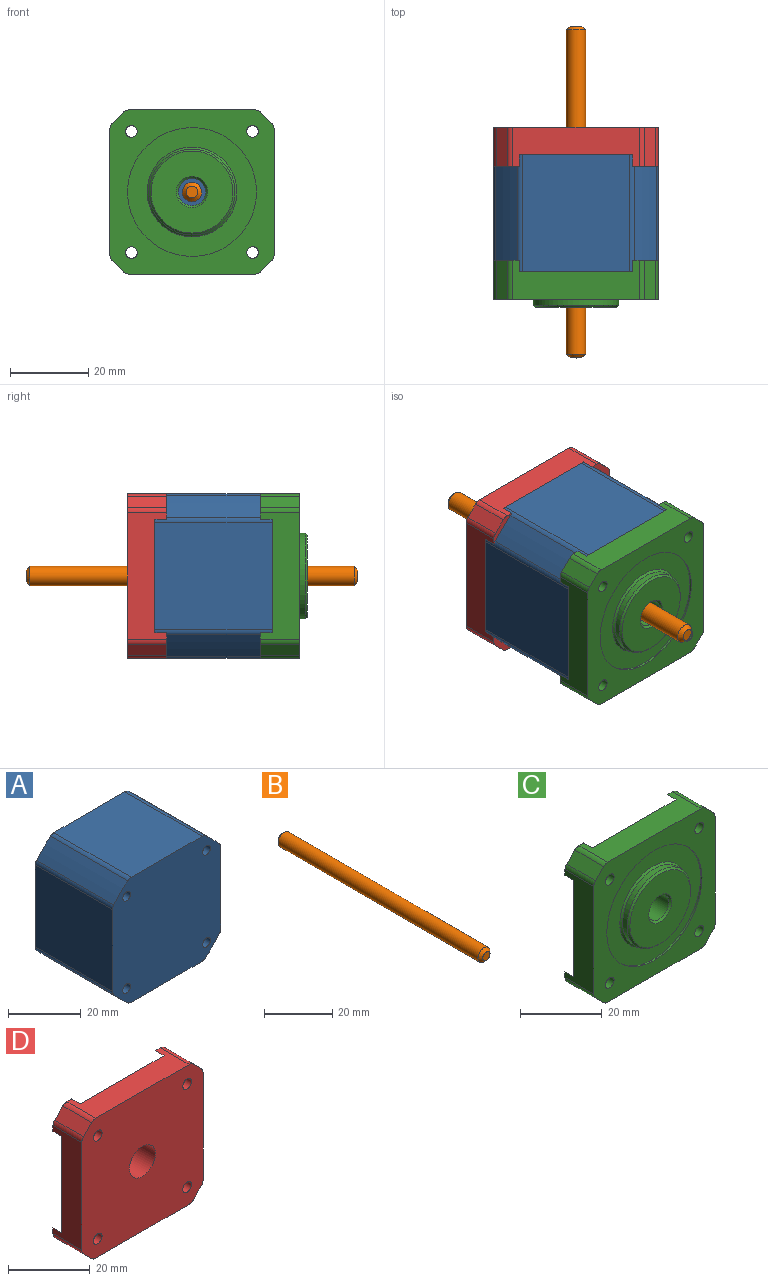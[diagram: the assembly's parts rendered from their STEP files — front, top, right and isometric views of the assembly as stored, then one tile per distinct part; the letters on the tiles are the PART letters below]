
ASSEMBLY  parts=4 mates=3
PART A: 22 faces, bbox 42x30x42 mm
  f0: cylinder r=55mm len=30mm, axis (0,1,0), area 230.4mm2, adj f8,f9,f10,f17
  f1: plane 30x27.54mm, normal (1,0,0), area 826.2mm2, adj f8,f9,f10,f11
  f2: cylinder r=55mm len=30mm, axis (0,1,0), area 230.4mm2, adj f8,f9,f11,f12
  f3: plane 30x27.54mm, normal (0,0,1), area 826.2mm2, adj f8,f9,f12,f13
  f4: cylinder r=55mm len=30mm, axis (0,1,0), area 230.4mm2, adj f8,f9,f13,f14
  f5: plane 30x27.54mm, normal (-1,0,0), area 826.2mm2, adj f8,f9,f14,f15
  f6: cylinder r=55mm len=30mm, axis (0,1,0), area 230.4mm2, adj f8,f9,f15,f16
  f7: plane 30x27.54mm, normal (0,0,-1), area 826.2mm2, adj f8,f9,f16,f17
  f8: plane 42x42mm, normal (0,-1,0), area 1655.7mm2, adj f0,f1,f2,f3,f4,f5,f6,f7
  f9: plane 42x42mm, normal (0,1,0), area 1655.7mm2, adj f0,f1,f2,f3,f4,f5,f6,f7
  f10: cylinder r=2mm len=30mm, axis (0,1,0), area 42.9mm2, adj f0,f1,f8,f9
  f11: cylinder r=2mm len=30mm, axis (0,1,0), area 42.9mm2, adj f1,f2,f8,f9
  f12: cylinder r=2mm len=30mm, axis (0,1,0), area 42.9mm2, adj f2,f3,f8,f9
  f13: cylinder r=2mm len=30mm, axis (0,1,0), area 42.9mm2, adj f3,f4,f8,f9
  f14: cylinder r=2mm len=30mm, axis (0,1,0), area 42.9mm2, adj f4,f5,f8,f9
  f15: cylinder r=2mm len=30mm, axis (0,1,0), area 42.9mm2, adj f5,f6,f8,f9
  f16: cylinder r=2mm len=30mm, axis (0,1,0), area 42.9mm2, adj f6,f7,f8,f9
  f17: cylinder r=2mm len=30mm, axis (0,1,0), area 42.9mm2, adj f0,f7,f8,f9
  f18: cylinder r=1.5mm len=30mm, axis (0,-1,0), area 282.7mm2, adj f8,f9
  f19: cylinder r=1.5mm len=30mm, axis (0,-1,0), area 282.7mm2, adj f8,f9
  f20: cylinder r=1.5mm len=30mm, axis (0,-1,0), area 282.7mm2, adj f8,f9
  f21: cylinder r=1.5mm len=30mm, axis (0,-1,0), area 282.7mm2, adj f8,f9
PART B: 5 faces, bbox 5x85x5 mm
  f0: cylinder r=2.5mm len=83mm, axis (0,1,0), area 1303.8mm2, adj f3,f4
  f1: plane 3x3mm, normal (0,-1,0), area 7.1mm2, adj f4
  f2: plane 3x3mm, normal (0,1,0), area 7.1mm2, adj f3
  f3: cone r=2.5mm half-angle=45deg, axis (0,-1,0), area 17.8mm2, adj f0,f2
  f4: cone r=1.5mm half-angle=45deg, axis (0,1,0), area 17.8mm2, adj f0,f1
PART C: 38 faces, bbox 42x12x42 mm
  f0: plane 32.34x10mm, normal (1,0,0), area 236.4mm2, adj f3,f4,f9,f20,f21,f29,f31,f32
  f1: plane 32.34x10mm, normal (0,0,1), area 236.4mm2, adj f2,f3,f9,f18,f19,f29,f30,f31
  f2: plane 6.49x6.49mm, normal (0,1,0), area 11.7mm2, adj f1,f7,f13,f19,f23,f30
  f3: plane 6.49x6.49mm, normal (0,1,0), area 11.7mm2, adj f0,f1,f12,f18,f21,f31
  f4: plane 6.49x6.49mm, normal (0,1,0), area 11.7mm2, adj f0,f8,f11,f20,f25,f32
  f5: plane 6.49x6.49mm, normal (0,1,0), area 11.7mm2, adj f7,f8,f10,f22,f24,f33
  f6: cylinder r=3.5mm len=8.5mm, axis (0,-1,0), area 186.9mm2, adj f27,f29
  f7: plane 32.34x10mm, normal (-1,0,0), area 236.4mm2, adj f2,f5,f9,f22,f23,f29,f30,f33
  f8: plane 32.34x10mm, normal (0,0,-1), area 236.4mm2, adj f4,f5,f9,f24,f25,f29,f32,f33
  f9: plane 42x42mm, normal (0,-1,0), area 847.7mm2, adj f0,f1,f7,f8,f10,f11,f12,f13
  f10: plane 10x2.83mm, normal (-0.71,0,-0.71), area 40mm2, adj f5,f9,f22,f24
  f11: plane 10x2.83mm, normal (0.71,0,-0.71), area 40mm2, adj f4,f9,f20,f25
  f12: plane 10x2.83mm, normal (0.71,0,0.71), area 40mm2, adj f3,f9,f18,f21
  f13: plane 10x2.83mm, normal (-0.71,0,0.71), area 40mm2, adj f2,f9,f19,f23
  f14: cylinder r=16.5mm len=33mm, axis (0,-1,0), area 51.8mm2, adj f9,f15
  f15: plane 33x33mm, normal (0,-1,0), area 439.8mm2, adj f14,f26
  f16: cylinder r=11mm len=22mm, axis (0,1,0), area 103.7mm2, adj f26,f28
  f17: plane 21x21mm, normal (0,-1,0), area 296.1mm2, adj f27,f28
  f18: cylinder r=2mm len=10mm, axis (0,-1,0), area 15.7mm2, adj f1,f3,f9,f12
  f19: cylinder r=2mm len=10mm, axis (0,-1,0), area 15.7mm2, adj f1,f2,f9,f13
  f20: cylinder r=2mm len=10mm, axis (0,1,0), area 15.7mm2, adj f0,f4,f9,f11
  f21: cylinder r=2mm len=10mm, axis (0,1,0), area 15.7mm2, adj f0,f3,f9,f12
  f22: cylinder r=2mm len=10mm, axis (0,-1,0), area 15.7mm2, adj f5,f7,f9,f10
  f23: cylinder r=2mm len=10mm, axis (0,-1,0), area 15.7mm2, adj f2,f7,f9,f13
  f24: cylinder r=2mm len=10mm, axis (0,1,0), area 15.7mm2, adj f5,f8,f9,f10
  f25: cylinder r=2mm len=10mm, axis (0,1,0), area 15.7mm2, adj f4,f8,f9,f11
  f26: cone r=11mm half-angle=45deg, axis (0,1,0), area 50mm2, adj f15,f16
  f27: cone r=3.5mm half-angle=45deg, axis (0,-1,0), area 16.7mm2, adj f6,f17
  f28: cone r=10.5mm half-angle=45deg, axis (0,1,0), area 47.8mm2, adj f16,f17
  f29: plane 42x42mm, normal (0,1,0), area 1617.7mm2, adj f0,f1,f6,f7,f8,f30,f31,f32
  f30: cylinder r=55mm len=6.49mm, axis (0,1,0), area 27.6mm2, adj f1,f2,f7,f29
  f31: cylinder r=55mm len=6.49mm, axis (0,1,0), area 27.6mm2, adj f0,f1,f3,f29
  f32: cylinder r=55mm len=6.49mm, axis (0,1,0), area 27.6mm2, adj f0,f4,f8,f29
  f33: cylinder r=55mm len=6.49mm, axis (0,1,0), area 27.6mm2, adj f5,f7,f8,f29
  f34: cylinder r=1.5mm len=7mm, axis (0,-1,0), area 66mm2, adj f9,f29
  f35: cylinder r=1.5mm len=7mm, axis (0,-1,0), area 66mm2, adj f9,f29
  f36: cylinder r=1.5mm len=7mm, axis (0,-1,0), area 66mm2, adj f9,f29
  f37: cylinder r=1.5mm len=7mm, axis (0,-1,0), area 66mm2, adj f9,f29
PART D: 31 faces, bbox 42x10x42 mm
  f0: plane 32.34x10mm, normal (1,0,0), area 236.4mm2, adj f3,f4,f8,f15,f16,f22,f23,f25
  f1: plane 32.34x10mm, normal (0,0,1), area 236.4mm2, adj f2,f3,f8,f13,f14,f21,f22,f25
  f2: plane 6.49x6.49mm, normal (0,1,0), area 11.7mm2, adj f1,f6,f12,f14,f18,f21
  f3: plane 6.49x6.49mm, normal (0,1,0), area 11.7mm2, adj f0,f1,f11,f13,f16,f22
  f4: plane 6.49x6.49mm, normal (0,1,0), area 11.7mm2, adj f0,f7,f10,f15,f20,f23
  f5: plane 6.49x6.49mm, normal (0,1,0), area 11.7mm2, adj f6,f7,f9,f17,f19,f24
  f6: plane 32.34x10mm, normal (-1,0,0), area 236.4mm2, adj f2,f5,f8,f17,f18,f21,f24,f25
  f7: plane 32.34x10mm, normal (0,0,-1), area 236.4mm2, adj f4,f5,f8,f19,f20,f23,f24,f25
  f8: plane 42x42mm, normal (0,-1,0), area 1639.4mm2, adj f0,f1,f6,f7,f9,f10,f11,f12
  f9: plane 10x2.83mm, normal (-0.71,0,-0.71), area 40mm2, adj f5,f8,f17,f19
  f10: plane 10x2.83mm, normal (0.71,0,-0.71), area 40mm2, adj f4,f8,f15,f20
  f11: plane 10x2.83mm, normal (0.71,0,0.71), area 40mm2, adj f3,f8,f13,f16
  f12: plane 10x2.83mm, normal (-0.71,0,0.71), area 40mm2, adj f2,f8,f14,f18
  f13: cylinder r=2mm len=10mm, axis (0,-1,0), area 15.7mm2, adj f1,f3,f8,f11
  f14: cylinder r=2mm len=10mm, axis (0,-1,0), area 15.7mm2, adj f1,f2,f8,f12
  f15: cylinder r=2mm len=10mm, axis (0,1,0), area 15.7mm2, adj f0,f4,f8,f10
  f16: cylinder r=2mm len=10mm, axis (0,1,0), area 15.7mm2, adj f0,f3,f8,f11
  f17: cylinder r=2mm len=10mm, axis (0,-1,0), area 15.7mm2, adj f5,f6,f8,f9
  f18: cylinder r=2mm len=10mm, axis (0,-1,0), area 15.7mm2, adj f2,f6,f8,f12
  f19: cylinder r=2mm len=10mm, axis (0,1,0), area 15.7mm2, adj f5,f7,f8,f9
  f20: cylinder r=2mm len=10mm, axis (0,1,0), area 15.7mm2, adj f4,f7,f8,f10
  f21: cylinder r=55mm len=6.49mm, axis (0,1,0), area 27.6mm2, adj f1,f2,f6,f25
  f22: cylinder r=55mm len=6.49mm, axis (0,1,0), area 27.6mm2, adj f0,f1,f3,f25
  f23: cylinder r=55mm len=6.49mm, axis (0,1,0), area 27.6mm2, adj f0,f4,f7,f25
  f24: cylinder r=55mm len=6.49mm, axis (0,1,0), area 27.6mm2, adj f5,f6,f7,f25
  f25: plane 42x42mm, normal (0,1,0), area 1592.6mm2, adj f0,f1,f6,f7,f21,f22,f23,f24
  f26: cylinder r=1.5mm len=7mm, axis (0,-1,0), area 66mm2, adj f8,f25
  f27: cylinder r=1.5mm len=7mm, axis (0,-1,0), area 66mm2, adj f8,f25
  f28: cylinder r=1.5mm len=7mm, axis (0,-1,0), area 66mm2, adj f8,f25
  f29: cylinder r=1.5mm len=7mm, axis (0,-1,0), area 66mm2, adj f8,f25
  f30: cylinder r=4.5mm len=9mm, axis (0,-1,0), area 197.9mm2, adj f8,f25
PLACE A t=(1.6,19.94,1.53)mm
PLACE B t=(1.6,25.44,1.53)mm
PLACE C t=(1.6,7.94,1.53)mm fixed
PLACE D rot(axis=(0,0,1),180deg) t=(1.6,31.94,1.53)mm
MATE fastened A.f19 <-> C.f34  axis (0,-1,0) through (-13.9,4.94,17.03)mm
MATE revolute B.f0 <-> C.f6  axis (0,-1,0) through (1.6,-17.06,1.53)mm
MATE fastened D.f29 <-> A.f19  axis (0,-1,0) through (-13.9,34.94,17.03)mm
